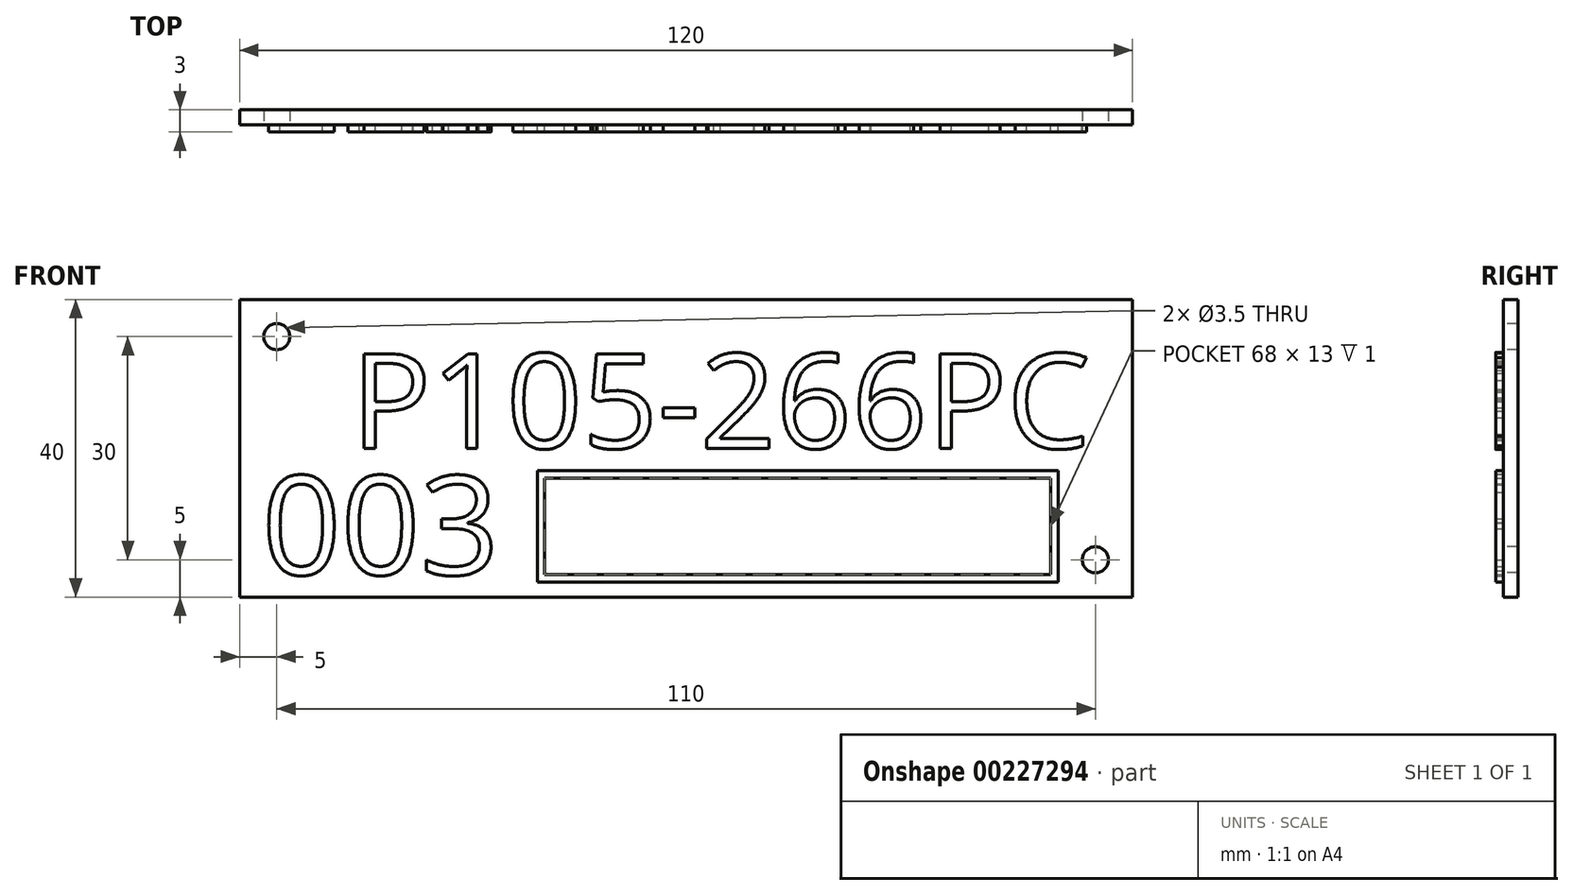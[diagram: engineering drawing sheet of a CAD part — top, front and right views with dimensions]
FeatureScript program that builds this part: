
annotation { "Feature Type Name" : "Feature", "Feature Type Description" : "" }
export const myFeature = defineFeature(function(context is Context, id is Id, definition is map)
    precondition{}
    {
        {
            var Q0;
            Q0=qCreatedBy(makeId("Front.planeOp"),FACE);
            var sketch = newSketch(context, id + "F0", { "sketchPlane" : qUnion([Q0])});
            skLineSegment(sketch, "E0.bottom", {"start": v(60, -20) * mm, "end": v(-60, -20) * mm});
            skLineSegment(sketch, "E0.top", {"start": v(60, 20) * mm, "end": v(-60, 20) * mm});
            skLineSegment(sketch, "E0.left", {"start": v(60, -20) * mm, "end": v(60, 20) * mm});
            skLineSegment(sketch, "E0.right", {"start": v(-60, -20) * mm, "end": v(-60, 20) * mm});
            skPoint(sketch, "E0.middle", {"position": v(0, 0) * mm});
            skSolve(sketch);
        }
        {
            var Q0;
            Q0=makeQuery(id+"F0.imprint","IMPRINT",FACE,{"disambiguationData":[TD([[makeQuery(id+"F0.imprint","IMPRINT",EDGE,{"derivedFrom":sQuery(id+"F0.wireOp",EDGE,"E0.bottom")}),-1.0]])]});
            extrude(context, id + "F1", {"entities" : qUnion([Q0]), "depth" : 2 * mm});
        }
        {
            var Q0;
            Q0=makeQuery(id+"F1.opExtrude","CAP_FACE",FACE,{"disambiguationData":[OSD([sQuery(id+"F0.wireOp",EDGE,"E0.bottom"),sQuery(id+"F0.wireOp",EDGE,"E0.top"),sQuery(id+"F0.wireOp",EDGE,"E0.left"),sQuery(id+"F0.wireOp",EDGE,"E0.right")])],"isStart":false});
            var sketch = newSketch(context, id + "F2", { "sketchPlane" : qUnion([Q0])});
            skPoint(sketch, "E1", {"position": v(-55, 15) * mm});
            skPoint(sketch, "E2", {"position": v(55, -15) * mm});
            skSolve(sketch);
        }
        {
            var Q0;
            Q0=sQuery(id+"F2.wireOp",VERTEX,"E1");
            var Q1;
            Q1=sQuery(id+"F2.wireOp",VERTEX,"E2");
            var Q2;
            Q2=makeQuery(id+"F1.opExtrude","SWEPT_BODY",BODY,{"disambiguationData":[OSD([sQuery(id+"F0.wireOp",EDGE,"E0.bottom"),sQuery(id+"F0.wireOp",EDGE,"E0.top"),sQuery(id+"F0.wireOp",EDGE,"E0.left"),sQuery(id+"F0.wireOp",EDGE,"E0.right")])]});
            hole(context, id + "F3", {"style" : HoleStyle.SIMPLE, "endStyle" : HoleEndStyle.THROUGH, "holeDiameter" : 3.5 * mm, "locations" : qUnion([Q0, Q1]), "scope" : qUnion([Q2]), "isTappedThrough" : true});
        }
        {
            var Q0;
            Q0=makeQuery(id+"F1.opExtrude","CAP_FACE",FACE,{"disambiguationData":[OSD([sQuery(id+"F0.wireOp",EDGE,"E0.bottom"),sQuery(id+"F0.wireOp",EDGE,"E0.top"),sQuery(id+"F0.wireOp",EDGE,"E0.left"),sQuery(id+"F0.wireOp",EDGE,"E0.right")])],"isStart":false});
            var sketch = newSketch(context, id + "F4", { "sketchPlane" : qUnion([Q0])});
            skText(sketch, "E3", { "text": "P105-266PC", "fontName": "OpenSans-Regular.ttf"});
            const initialGuessF4  = {"E3": [-0.045, 0, 1, 0, 0.0128]};
            skSetInitialGuess(sketch, initialGuessF4);
            skSolve(sketch);
        }
        {
            var Q0;
            Q0 = qSketchRegion(id + "F4", true);
            extrude(context, id + "F5", {"entities" : qUnion([Q0]), "operationType" : NewBodyOperationType.ADD, "depth" : 1 * mm});
        }
        {
            var Q0;
            {var subQ0=sQuery(id+"F0.wireOp",EDGE,"E0.top");var subQ1=sQuery(id+"F0.wireOp",EDGE,"E0.left");var subQ2=sQuery(id+"F0.wireOp",EDGE,"E0.right");var subQ3=sQuery(id+"F0.wireOp",EDGE,"E0.bottom");Q0=makeQuery(id+"F5.boolean.opBoolean","SPLIT",FACE,{"disambiguationData":[TD([makeQuery(id+"F1.opExtrude","SWEPT_FACE",FACE,{"disambiguationData":[OSD([subQ3])]})])],"derivedFrom":makeQuery(id+"F1.opExtrude","CAP_FACE",FACE,{"disambiguationData":[OSD([subQ3,subQ0,subQ1,subQ2])],"isStart":false})});}
            var sketch = newSketch(context, id + "F6", { "sketchPlane" : qUnion([Q0])});
            skText(sketch, "E4", { "text": "003", "fontName": "OpenSans-Regular.ttf"});
            const initialGuessF6  = {"E4": [-0.057, -0.017, 1, 0, 0.01338]};
            skSetInitialGuess(sketch, initialGuessF6);
            skSolve(sketch);
        }
        {
            var Q0;
            Q0 = qSketchRegion(id + "F6", true);
            extrude(context, id + "F7", {"entities" : qUnion([Q0]), "operationType" : NewBodyOperationType.ADD, "depth" : 1 * mm});
        }
        {
            var Q0;
            {var subQ49=sQuery(id+"F0.wireOp",EDGE,"E0.top");var subQ51=sQuery(id+"F0.wireOp",EDGE,"E0.left");var subQ72=sQuery(id+"F0.wireOp",EDGE,"E0.right");var subQ83=sQuery(id+"F0.wireOp",EDGE,"E0.bottom");var subQ84=makeQuery(id+"F1.opExtrude","SWEPT_FACE",FACE,{"disambiguationData":[OSD([subQ83])]});Q0=makeQuery(id+"F7.boolean.opBoolean","SPLIT",FACE,{"disambiguationData":[TD([subQ84])],"derivedFrom":makeQuery(id+"F5.boolean.opBoolean","SPLIT",FACE,{"disambiguationData":[TD([subQ84])],"derivedFrom":makeQuery(id+"F1.opExtrude","CAP_FACE",FACE,{"disambiguationData":[OSD([subQ83,subQ49,subQ51,subQ72])],"isStart":false})})});}
            var sketch = newSketch(context, id + "F8", { "sketchPlane" : qUnion([Q0])});
            skLineSegment(sketch, "E5.bottom", {"start": v(50, -18) * mm, "end": v(-20, -18) * mm});
            skLineSegment(sketch, "E5.top", {"start": v(50, -3) * mm, "end": v(-20, -3) * mm});
            skLineSegment(sketch, "E5.left", {"start": v(50, -18) * mm, "end": v(50, -3) * mm});
            skLineSegment(sketch, "E5.right", {"start": v(-20, -18) * mm, "end": v(-20, -3) * mm});
            skPoint(sketch, "E5.middle", {"position": v(15, -10.5) * mm});
            skLineSegment(sketch, "E6.0", {"start": v(-19, -17) * mm, "end": v(-19, -4) * mm});
            skLineSegment(sketch, "E6.1", {"start": v(49, -17) * mm, "end": v(-19, -17) * mm});
            skLineSegment(sketch, "E6.2", {"start": v(49, -17) * mm, "end": v(49, -4) * mm});
            skLineSegment(sketch, "E6.3", {"start": v(49, -4) * mm, "end": v(-19, -4) * mm});
            skSolve(sketch);
        }
        {
            var Q0;
            Q0=makeQuery(id+"F8.imprint","IMPRINT",FACE,{"disambiguationData":[TD([[makeQuery(id+"F8.imprint","IMPRINT",EDGE,{"derivedFrom":sQuery(id+"F8.wireOp",EDGE,"E5.bottom")}),-1.0]])]});
            extrude(context, id + "F9", {"entities" : qUnion([Q0]), "operationType" : NewBodyOperationType.ADD, "depth" : 1 * mm});
        }
    });
